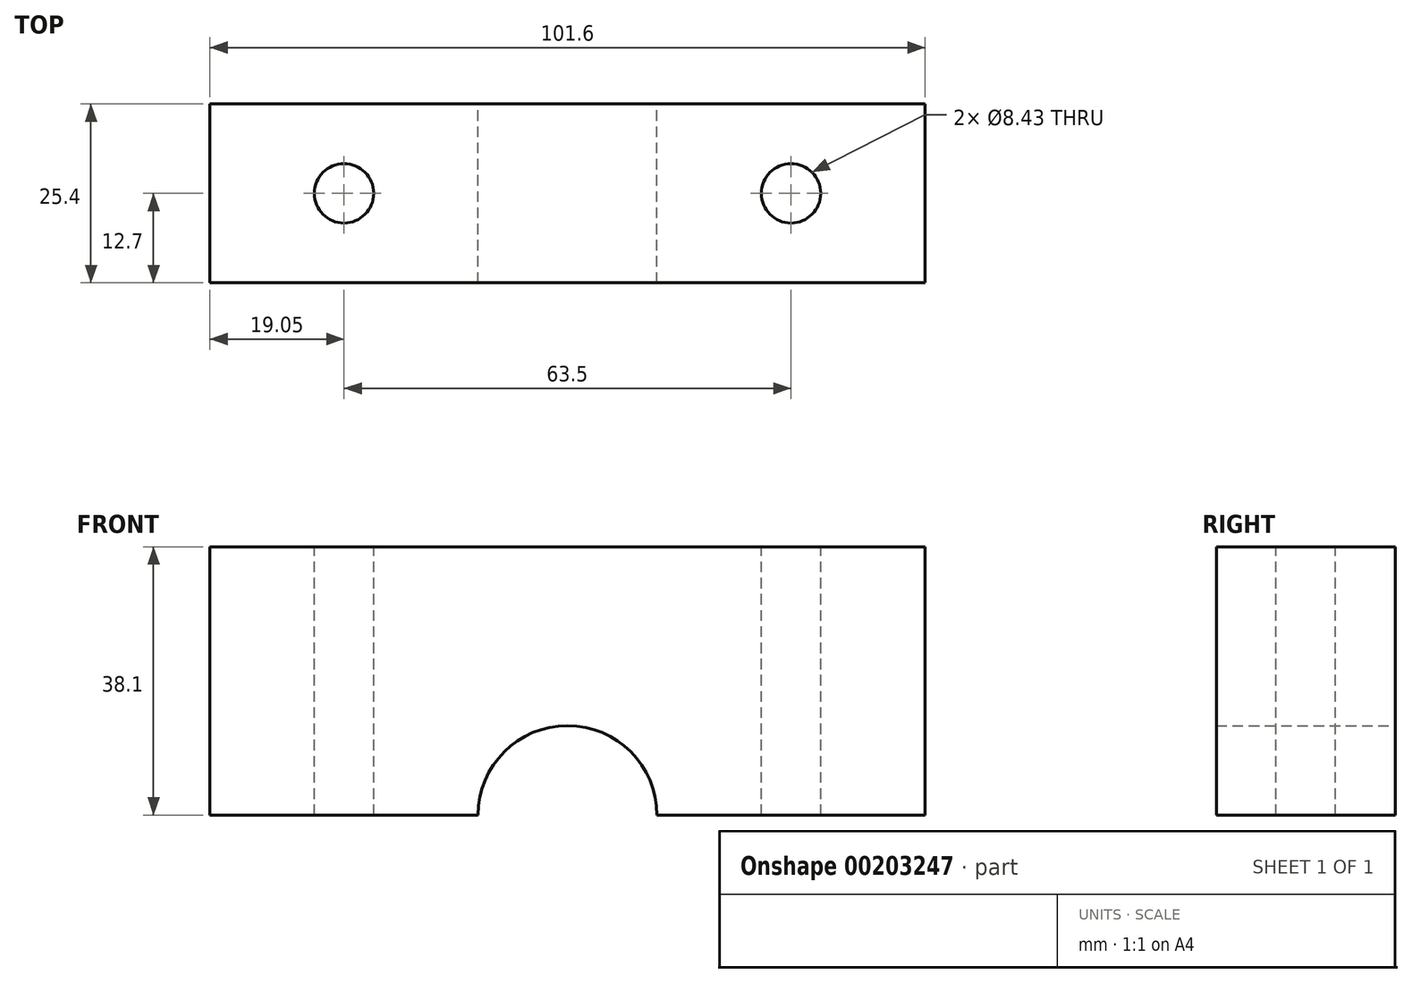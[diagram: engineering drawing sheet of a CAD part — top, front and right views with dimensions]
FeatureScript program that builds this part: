
annotation { "Feature Type Name" : "Feature", "Feature Type Description" : "" }
export const myFeature = defineFeature(function(context is Context, id is Id, definition is map)
    precondition{}
    {
        {
            var Q0;
            Q0=qCreatedBy(makeId("Front.planeOp"),FACE);
            var sketch = newSketch(context, id + "F0", { "sketchPlane" : qUnion([Q0])});
            skLineSegment(sketch, "E0.bottom", {"start": v(0, 0) * mm, "end": v(38.1, 0) * mm});
            skLineSegment(sketch, "E0.top", {"start": v(0, 38.1) * mm, "end": v(101.6, 38.1) * mm});
            skLineSegment(sketch, "E0.left", {"start": v(0, 0) * mm, "end": v(0, 38.1) * mm});
            skLineSegment(sketch, "E0.right", {"start": v(101.6, 0) * mm, "end": v(101.6, 38.1) * mm});
            skArc(sketch, "E1", {"start": v(63.5, 0) * mm, "mid": v(50.8, 12.7) * mm, "end": v(38.1, 0) * mm});
            skLineSegment(sketch, "E2.trimOffspring", {"start": v(63.5, 0) * mm, "end": v(101.6, 0) * mm});
            skSolve(sketch);
        }
        {
            var Q0;
            Q0 = qSketchRegion(id + "F0", true);
            extrude(context, id + "F1", {"entities" : qUnion([Q0]), "depth" : 25.4 * mm});
        }
        {
            var Q0;
            Q0=makeQuery(id+"F1.opExtrude","SWEPT_FACE",FACE,{"disambiguationData":[OSD([sQuery(id+"F0.wireOp",EDGE,"E0.top")])]});
            var sketch = newSketch(context, id + "F2", { "sketchPlane" : qUnion([Q0])});
            skPoint(sketch, "E3", {"position": v(19.05, -12.7) * mm});
            skPoint(sketch, "E4", {"position": v(82.55, -12.7) * mm});
            skSolve(sketch);
        }
        {
            var Q0;
            Q0=sQuery(id+"F2.wireOp",VERTEX,"E3");
            var Q1;
            Q1=sQuery(id+"F2.wireOp",VERTEX,"E4");
            var Q2;
            Q2=makeQuery(id+"F1.opExtrude","SWEPT_BODY",BODY,{"disambiguationData":[OSD([sQuery(id+"F0.wireOp",EDGE,"E0.bottom"),sQuery(id+"F0.wireOp",EDGE,"E0.top"),sQuery(id+"F0.wireOp",EDGE,"E0.left"),sQuery(id+"F0.wireOp",EDGE,"E0.right"),sQuery(id+"F0.wireOp",EDGE,"E1"),sQuery(id+"F0.wireOp",EDGE,"E2.trimOffspring")])]});
            hole(context, id + "F3", {"style" : HoleStyle.SIMPLE, "endStyle" : HoleEndStyle.THROUGH, "standardTappedOrClearance" : lookupTablePath({ "standard" : "ANSI", "engagement" : "75%", "pitch" : "24 tpi", "size" : "3/8", "type" : "Tapped" }), "standardBlindInLast" : lookupTablePath({ "standard" : "ANSI", "engagement" : "75%", "pitch" : "24 tpi", "size" : "3/8", "type" : "Tapped" }), "holeDiameter" : 8.43 * mm, "startFromSketch" : true, "locations" : qUnion([Q0, Q1]), "scope" : qUnion([Q2]), "isTappedThrough" : true, "majorDiameter" : 9.53 * mm, "showTappedDepth" : true});
        }
    });
